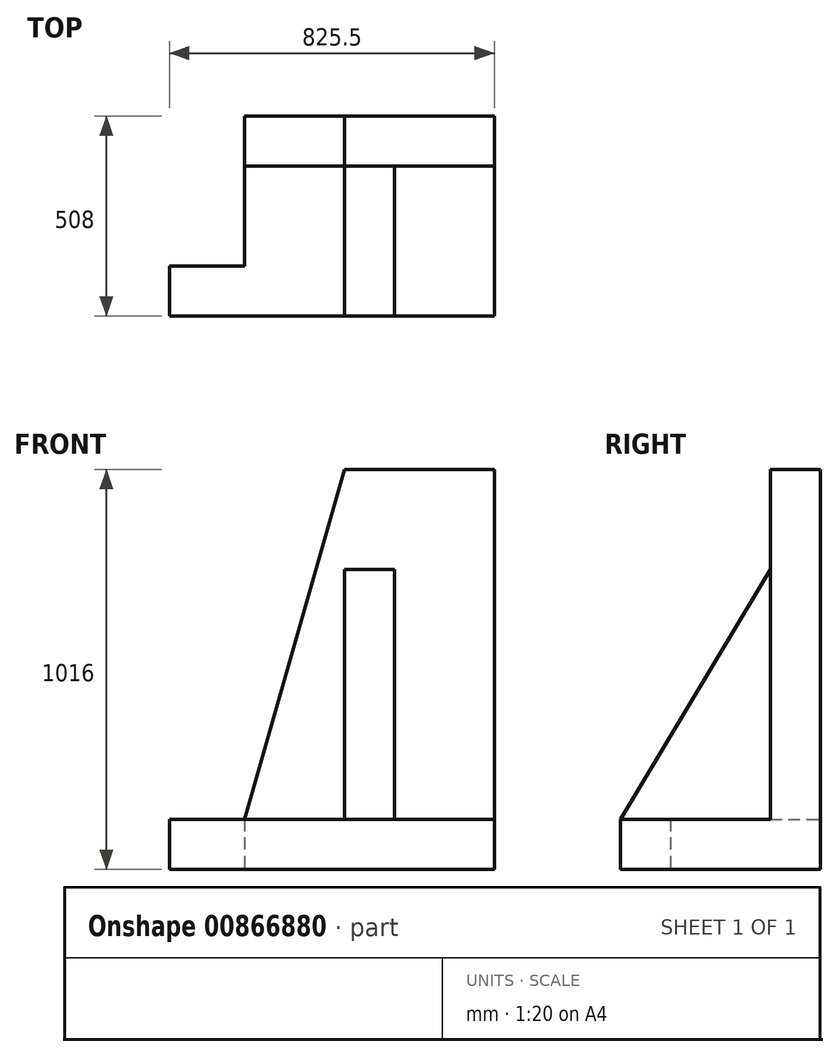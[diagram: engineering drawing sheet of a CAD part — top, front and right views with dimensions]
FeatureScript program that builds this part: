
annotation { "Feature Type Name" : "Feature", "Feature Type Description" : "" }
export const myFeature = defineFeature(function(context is Context, id is Id, definition is map)
    precondition{}
    {
        {
            var Q0;
            Q0=qCreatedBy(makeId("Top.planeOp"),FACE);
            var sketch = newSketch(context, id + "F0", { "sketchPlane" : qUnion([Q0])});
            skLineSegment(sketch, "E0.bottom", {"start": v(79.42, 0) * mm, "end": v(714.42, 0) * mm});
            skLineSegment(sketch, "E0.top", {"start": v(79.42, 508) * mm, "end": v(714.42, 508) * mm});
            skLineSegment(sketch, "E0.left", {"start": v(79.42, 0) * mm, "end": v(79.42, 508) * mm});
            skLineSegment(sketch, "E0.right", {"start": v(714.42, 0) * mm, "end": v(714.42, 508) * mm});
            skLineSegment(sketch, "E1.bottom", {"start": v(79.42, 0) * mm, "end": v(-111.08, 0) * mm});
            skLineSegment(sketch, "E1.top", {"start": v(79.42, 127) * mm, "end": v(-111.08, 127) * mm});
            skLineSegment(sketch, "E1.left", {"start": v(79.42, 0) * mm, "end": v(79.42, 127) * mm});
            skLineSegment(sketch, "E1.right", {"start": v(-111.08, 0) * mm, "end": v(-111.08, 127) * mm});
            skSolve(sketch);
        }
        {
            var Q0;
            {var subQ1=sQuery(id+"F0.wireOp",EDGE,"E0.bottom");Q0=makeQuery(id+"F0.imprint","IMPRINT",FACE,{"disambiguationData":[TD([[makeQuery(id+"F0.imprint","IMPRINT",EDGE,{"derivedFrom":subQ1}),1.0]])]});}
            var Q1;
            {var subQ0=sQuery(id+"F0.wireOp",EDGE,"E1.bottom");Q1=makeQuery(id+"F0.imprint","IMPRINT",FACE,{"disambiguationData":[TD([[makeQuery(id+"F0.imprint","IMPRINT",EDGE,{"derivedFrom":subQ0}),-1.0]])]});}
            extrude(context, id + "F1", {"entities" : qUnion([Q0, Q1]), "depth" : 127 * mm, "offsetDistance" : 25.4 * mm});
        }
        {
            var Q0;
            Q0=makeQuery(id+"F1.opExtrude","SWEPT_FACE",FACE,{"disambiguationData":[OSD([sQuery(id+"F0.wireOp",EDGE,"E0.top")])]});
            var sketch = newSketch(context, id + "F2", { "sketchPlane" : qUnion([Q0])});
            skLineSegment(sketch, "E2.bottom", {"start": v(-714.42, 0) * mm, "end": v(-333.42, 0) * mm});
            skLineSegment(sketch, "E2.top", {"start": v(-714.42, 1016) * mm, "end": v(-333.42, 1016) * mm});
            skLineSegment(sketch, "E2.left", {"start": v(-714.42, 0) * mm, "end": v(-714.42, 1016) * mm});
            skLineSegment(sketch, "E2.right", {"start": v(-333.42, 0) * mm, "end": v(-333.42, 1016) * mm});
            skLineSegment(sketch, "E3", {"start": v(-333.42, 1016) * mm, "end": v(-79.42, 127) * mm});
            skSolve(sketch);
        }
        {
            var Q0;
            {var subQ0=sQuery(id+"F2.wireOp",EDGE,"E2.top");Q0=makeQuery(id+"F2.imprint","IMPRINT",FACE,{"disambiguationData":[TD([[makeQuery(id+"F2.imprint","IMPRINT",EDGE,{"derivedFrom":subQ0}),-1.0]])]});}
            var Q1;
            {var subQ0=sQuery(id+"F2.wireOp",EDGE,"E3");Q1=makeQuery(id+"F2.imprint","IMPRINT",FACE,{"disambiguationData":[TD([[makeQuery(id+"F2.imprint","IMPRINT",EDGE,{"derivedFrom":subQ0}),-1.0]])]});}
            extrude(context, id + "F3", {"entities" : qUnion([Q0, Q1]), "operationType" : NewBodyOperationType.ADD, "oppositeDirection" : true, "depth" : 127 * mm, "offsetDistance" : 25.4 * mm});
        }
        {
            var Q0;
            Q0=makeQuery(id+"F3.opExtrude","CAP_FACE",FACE,{"disambiguationData":[OSD([sQuery(id+"F0.wireOp",EDGE,"E0.top"),sQuery(id+"F2.wireOp",EDGE,"E2.top"),sQuery(id+"F2.wireOp",EDGE,"E2.left"),sQuery(id+"F2.wireOp",EDGE,"E3")])],"isStart":false});
            var sketch = newSketch(context, id + "F4", { "sketchPlane" : qUnion([Q0])});
            skLineSegment(sketch, "E4.bottom", {"start": v(714.42, 127) * mm, "end": v(460.42, 127) * mm});
            skLineSegment(sketch, "E4.top", {"start": v(714.42, 762) * mm, "end": v(460.42, 762) * mm});
            skLineSegment(sketch, "E4.left", {"start": v(714.42, 127) * mm, "end": v(714.42, 762) * mm});
            skLineSegment(sketch, "E4.right", {"start": v(460.42, 127) * mm, "end": v(460.42, 762) * mm});
            skLineSegment(sketch, "E5.bottom", {"start": v(460.42, 127) * mm, "end": v(333.42, 127) * mm});
            skLineSegment(sketch, "E5.top", {"start": v(460.42, 762) * mm, "end": v(333.42, 762) * mm});
            skLineSegment(sketch, "E5.right", {"start": v(333.42, 127) * mm, "end": v(333.42, 762) * mm});
            skSolve(sketch);
        }
        {
            var Q0;
            Q0=makeQuery(id+"F4.imprint","IMPRINT",FACE,{"disambiguationData":[TD([[makeQuery(id+"F4.imprint","IMPRINT",EDGE,{"derivedFrom":sQuery(id+"F4.wireOp",EDGE,"E5.bottom")}),1.0]])]});
            var Q1;
            Q1=makeQuery(id+"F1.opExtrude","SWEPT_FACE",FACE,{"disambiguationData":[OSD([sQuery(id+"F0.wireOp",EDGE,"E0.bottom"),sQuery(id+"F0.wireOp",EDGE,"E1.bottom")])]});
            extrude(context, id + "F5", {"entities" : qUnion([Q0]), "operationType" : NewBodyOperationType.ADD, "endBound" : BoundingType.UP_TO_SURFACE, "depth" : 60.96 * mm, "endBoundEntityFace" : qUnion([Q1]), "offsetDistance" : 25.4 * mm});
        }
        {
            var Q0;
            Q0=makeQuery(id+"F5.opExtrude","SWEPT_FACE",FACE,{"disambiguationData":[OSD([sQuery(id+"F4.wireOp",EDGE,"E5.right")])]});
            var sketch = newSketch(context, id + "F6", { "sketchPlane" : qUnion([Q0])});
            skLineSegment(sketch, "E6", {"start": v(-381, 762) * mm, "end": v(0, 127) * mm});
            skSolve(sketch);
        }
        {
            var Q0;
            Q0=makeQuery(id+"F6.imprint","IMPRINT",FACE,{"disambiguationData":[TD([[makeQuery(id+"F6.imprint","IMPRINT",EDGE,{"derivedFrom":sQuery(id+"F6.wireOp",EDGE,"E6")}),1.0]])]});
            extrude(context, id + "F7", {"entities" : qUnion([Q0]), "operationType" : NewBodyOperationType.REMOVE, "endBound" : BoundingType.THROUGH_ALL, "oppositeDirection" : true, "depth" : 25.4 * mm, "offsetDistance" : 25.4 * mm});
        }
    });
